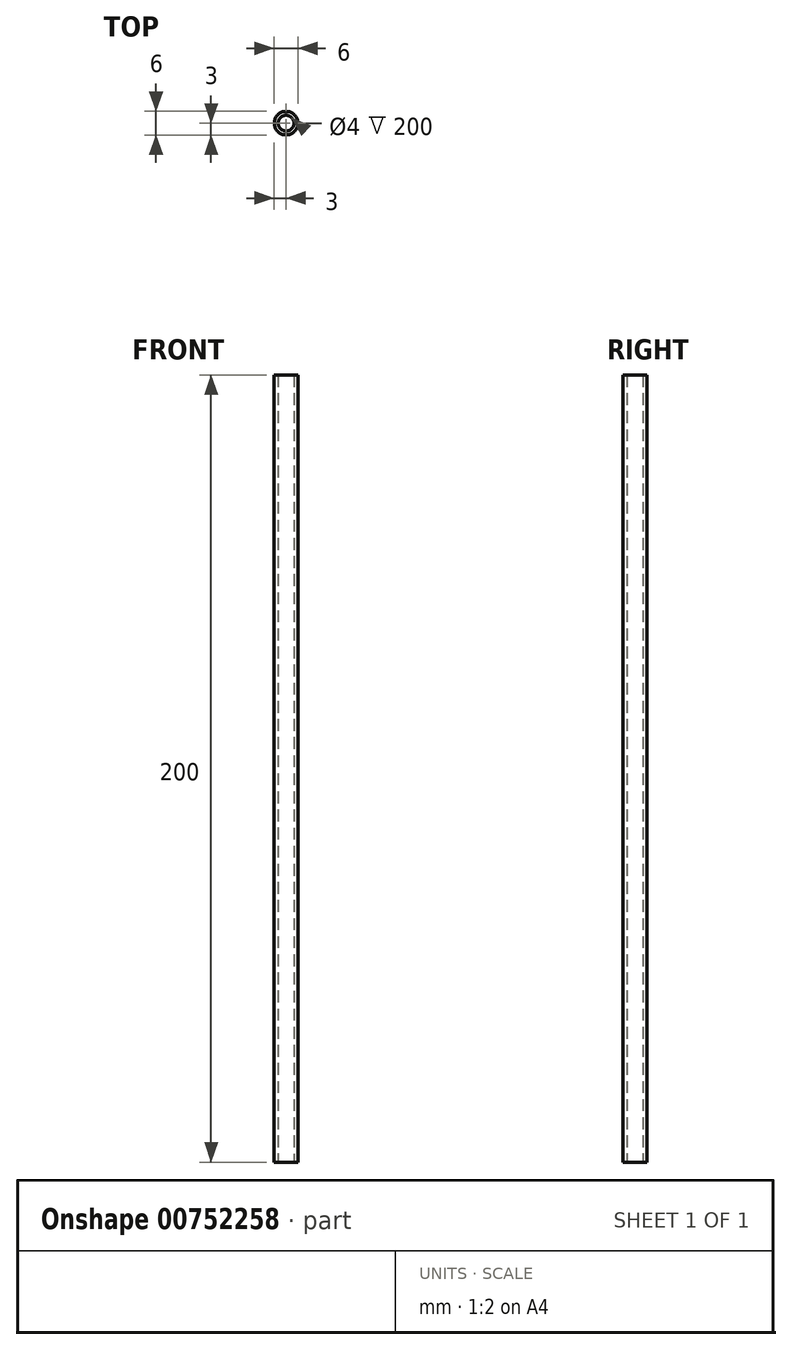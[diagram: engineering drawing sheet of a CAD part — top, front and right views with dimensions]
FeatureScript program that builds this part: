
annotation { "Feature Type Name" : "Feature", "Feature Type Description" : "" }
export const myFeature = defineFeature(function(context is Context, id is Id, definition is map)
    precondition{}
    {
        {
            var Q0;
            Q0=qCreatedBy(makeId("Top.planeOp"),FACE);
            var sketch = newSketch(context, id + "F0", { "sketchPlane" : qUnion([Q0])});
            skCircle(sketch, "E0", {"center": v(0, 0) * mm, "radius": 2 * mm});
            skCircle(sketch, "E1", {"center": v(0, 0) * mm, "radius": 3 * mm});
            skSolve(sketch);
        }
        {
            var Q0;
            Q0=makeQuery(id+"F0.imprint","IMPRINT",FACE,{"disambiguationData":[TD([[makeQuery(id+"F0.imprint","IMPRINT",EDGE,{"derivedFrom":sQuery(id+"F0.wireOp",EDGE,"E0")}),-1.0]])]});
            extrude(context, id + "F1", {"entities" : qUnion([Q0]), "depth" : 200 * mm, "offsetDistance" : 25 * mm});
        }
    });
